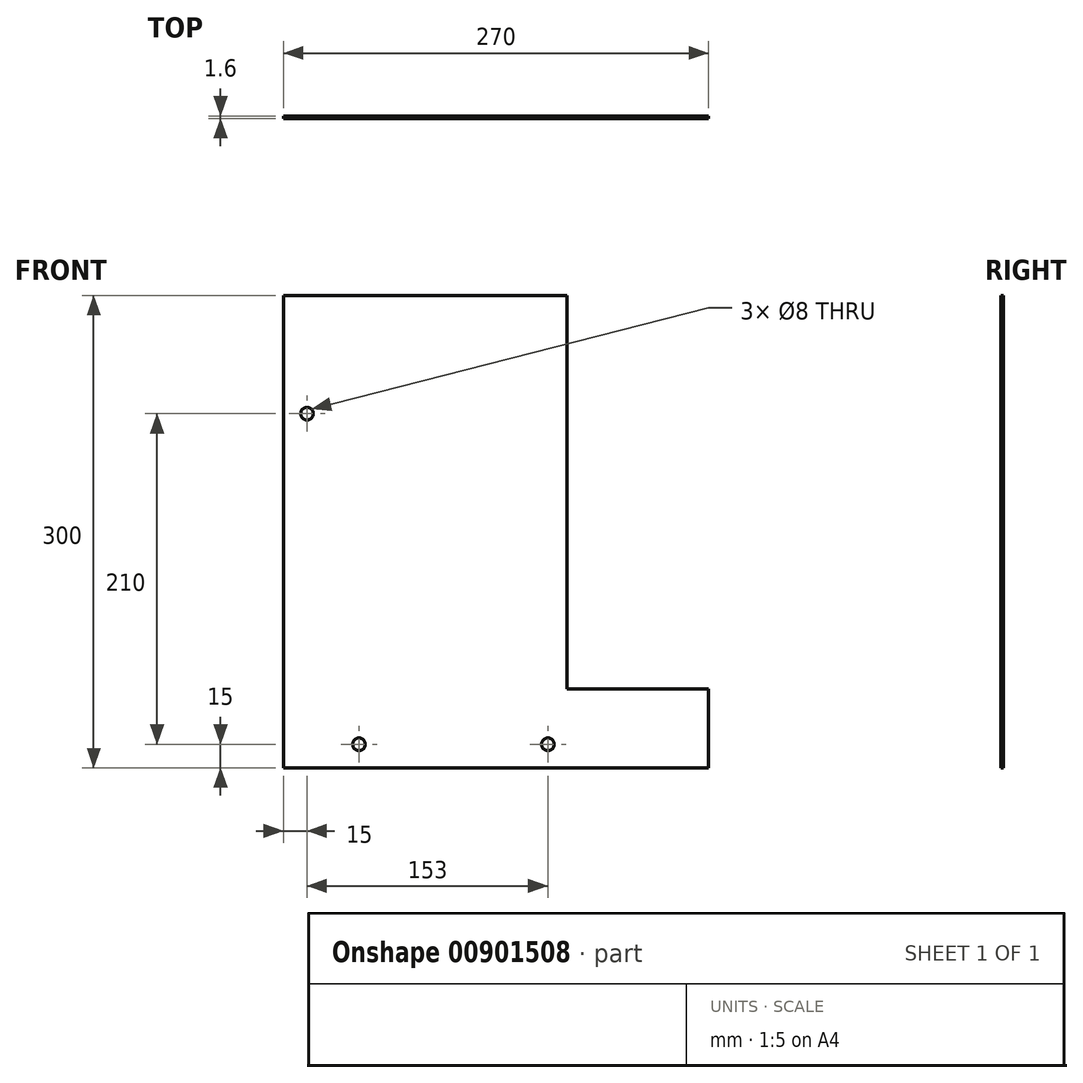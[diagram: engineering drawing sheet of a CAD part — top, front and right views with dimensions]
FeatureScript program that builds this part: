
annotation { "Feature Type Name" : "Feature", "Feature Type Description" : "" }
export const myFeature = defineFeature(function(context is Context, id is Id, definition is map)
    precondition{}
    {
        {
            var Q0;
            Q0=qCreatedBy(makeId("Front.planeOp"),FACE);
            var sketch = newSketch(context, id + "F0", { "sketchPlane" : qUnion([Q0])});
            skLineSegment(sketch, "E0", {"start": v(0, 0) * mm, "end": v(0, -300) * mm});
            skLineSegment(sketch, "E1", {"start": v(0, -300) * mm, "end": v(270, -300) * mm});
            skLineSegment(sketch, "E2", {"start": v(270, -300) * mm, "end": v(270, -250) * mm});
            skLineSegment(sketch, "E3", {"start": v(270, -250) * mm, "end": v(180, -250) * mm});
            skLineSegment(sketch, "E4", {"start": v(180, -250) * mm, "end": v(180, 0) * mm});
            skLineSegment(sketch, "E5", {"start": v(180, 0) * mm, "end": v(0, 0) * mm});
            skPoint(sketch, "E6", {"position": v(48, -285) * mm});
            skPoint(sketch, "E7", {"position": v(168, -285) * mm});
            skPoint(sketch, "E8", {"position": v(15, -75) * mm});
            skSolve(sketch);
        }
        {
            var Q0;
            Q0=makeQuery(id+"F0.imprint","IMPRINT",FACE,{"disambiguationData":[TD([[makeQuery(id+"F0.imprint","IMPRINT",EDGE,{"derivedFrom":sQuery(id+"F0.wireOp",EDGE,"E0")}),1.0]])]});
            extrude(context, id + "F1", {"entities" : qUnion([Q0]), "depth" : 1.6 * mm, "offsetDistance" : 25 * mm});
        }
        {
            var Q0;
            Q0=sQuery(id+"F0.wireOp",VERTEX,"E8");
            var Q1;
            Q1=sQuery(id+"F0.wireOp",VERTEX,"E6");
            var Q2;
            Q2=sQuery(id+"F0.wireOp",VERTEX,"E7");
            var Q3;
            Q3=makeQuery(id+"F1.opExtrude","SWEPT_BODY",BODY,{"disambiguationData":[OSD([sQuery(id+"F0.wireOp",EDGE,"E0"),sQuery(id+"F0.wireOp",EDGE,"E1"),sQuery(id+"F0.wireOp",EDGE,"E2"),sQuery(id+"F0.wireOp",EDGE,"E3"),sQuery(id+"F0.wireOp",EDGE,"E4"),sQuery(id+"F0.wireOp",EDGE,"E5")])]});
            hole(context, id + "F2", {"style" : HoleStyle.SIMPLE, "endStyle" : HoleEndStyle.THROUGH, "oppositeDirection" : true, "standardTappedOrClearance" : lookupTablePath({ "standard" : "ISO", "size" : "8", "type" : "Drilled" }), "standardBlindInLast" : lookupTablePath({ "standard" : "ISO", "size" : "8", "type" : "Drilled" }), "holeDiameter" : 8 * mm, "majorDiameter" : 5 * mm, "isTappedThrough" : true, "tappedDepth" : 11.5 * mm, "tapClearance" : 3, "startFromSketch" : true, "locations" : qUnion([Q0, Q1, Q2]), "scope" : qUnion([Q3])});
        }
    });
